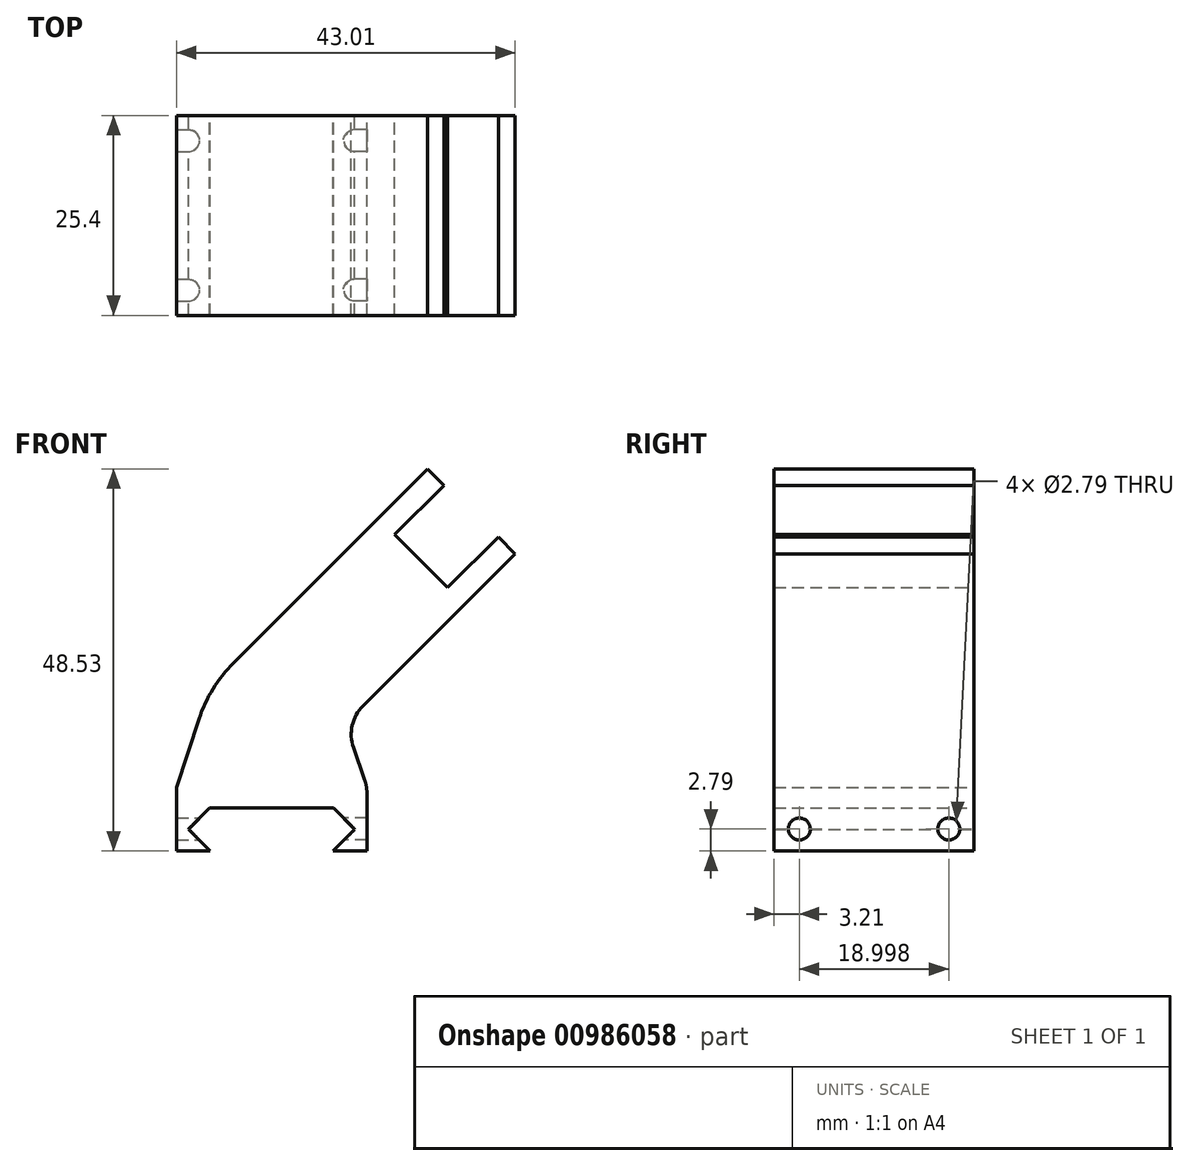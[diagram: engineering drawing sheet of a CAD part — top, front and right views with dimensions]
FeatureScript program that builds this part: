
annotation { "Feature Type Name" : "Feature", "Feature Type Description" : "" }
export const myFeature = defineFeature(function(context is Context, id is Id, definition is map)
    precondition{}
    {
        {
            var Q0;
            Q0=qCreatedBy(makeId("Front.planeOp"),FACE);
            var sketch = newSketch(context, id + "F0", { "sketchPlane" : qUnion([Q0])});
            skLineSegment(sketch, "E0", {"start": v(8.24, -9.31) * mm, "end": v(11, -6.54) * mm});
            skLineSegment(sketch, "E1", {"start": v(11, -6.54) * mm, "end": v(8.23, -3.78) * mm});
            skLineSegment(sketch, "E2.MirrorCS", {"start": v(-10.13, -6.54) * mm, "end": v(-7.35, -3.78) * mm});
            skLineSegment(sketch, "E3.MirrorCS", {"start": v(-7.36, -9.3) * mm, "end": v(-10.13, -6.54) * mm});
            skLineSegment(sketch, "E4.bottom", {"start": v(-7.36, -9.3) * mm, "end": v(-11.63, -9.3) * mm});
            skLineSegment(sketch, "E5.top", {"start": v(8.32, -3.86) * mm, "end": v(-7.44, -3.86) * mm});
            skLineSegment(sketch, "E6.right", {"start": v(-11.63, -1.23) * mm, "end": v(-11.63, -9.3) * mm});
            skLineSegment(sketch, "E7.top", {"start": v(12.55, -9.31) * mm, "end": v(8.24, -9.31) * mm});
            skLineSegment(sketch, "E7.left", {"start": v(12.55, -1.1) * mm, "end": v(12.55, -9.31) * mm});
            skLineSegment(sketch, "E8", {"start": v(9.8, 6.84) * mm, "end": v(12.55, -1.1) * mm});
            skLineSegment(sketch, "E9", {"start": v(-7.44, 11.55) * mm, "end": v(-11.63, -1.23) * mm});
            skLineSegment(sketch, "E10.top", {"start": v(16.07, 30.88) * mm, "end": v(22.8, 24.14) * mm});
            skLineSegment(sketch, "E10.left", {"start": v(-7.44, 11.55) * mm, "end": v(14.03, 33.02) * mm});
            skLineSegment(sketch, "E10.right", {"start": v(9.8, 6.84) * mm, "end": v(24.95, 22) * mm});
            skLineSegment(sketch, "E11.bottom", {"start": v(20.23, 39.22) * mm, "end": v(22.32, 37.13) * mm});
            skLineSegment(sketch, "E11.left", {"start": v(20.23, 39.22) * mm, "end": v(13.98, 32.97) * mm});
            skLineSegment(sketch, "E11.right", {"start": v(22.32, 37.13) * mm, "end": v(16.07, 30.88) * mm});
            skLineSegment(sketch, "E12.bottom", {"start": v(29.24, 30.58) * mm, "end": v(31.38, 28.44) * mm});
            skLineSegment(sketch, "E12.left", {"start": v(29.24, 30.58) * mm, "end": v(22.8, 24.14) * mm});
            skLineSegment(sketch, "E12.right", {"start": v(31.38, 28.44) * mm, "end": v(24.95, 22) * mm});
            skLineSegment(sketch, "E13.trimOffspring", {"start": v(-7.44, -1.2) * mm, "end": v(-7.44, -1.21) * mm});
            skPoint(sketch, "E14.top.end.orphan", {"position": v(-7.44, 8.88) * mm});
            skSolve(sketch);
        }
        {
            var Q0;
            {var subQ8=sQuery(id+"F0.wireOp",EDGE,"6de9e082-5b51-49be-9b5f-76bcd6000eec.right");Q0=makeQuery(id+"F0.imprint","IMPRINT",FACE,{"disambiguationData":[TD([[makeQuery(id+"F0.imprint","IMPRINT",EDGE,{"derivedFrom":subQ8}),1.0]])]});}
            var Q1;
            {var subQ6=sQuery(id+"F0.wireOp",EDGE,"E0");Q1=makeQuery(id+"F0.imprint","IMPRINT",FACE,{"disambiguationData":[TD([[makeQuery(id+"F0.imprint","IMPRINT",EDGE,{"derivedFrom":subQ6}),-1.0]])]});}
            var Q2;
            Q2=makeQuery(id+"F0.imprint","IMPRINT",FACE,{"disambiguationData":[TD([[makeQuery(id+"F0.imprint","IMPRINT",EDGE,{"derivedFrom":sQuery(id+"F0.wireOp",EDGE,"E11.bottom")}),-1.0]])]});
            var Q3;
            Q3=makeQuery(id+"F0.imprint","IMPRINT",FACE,{"disambiguationData":[TD([[makeQuery(id+"F0.imprint","IMPRINT",EDGE,{"derivedFrom":sQuery(id+"F0.wireOp",EDGE,"E12.bottom")}),-1.0]])]});
            extrude(context, id + "F1", {"entities" : qUnion([Q0, Q1, Q2, Q3]), "depth" : 25.4 * mm, "offsetDistance" : 25.4 * mm});
        }
        {
            var Q0;
            Q0=qCreatedBy(makeId("Right.planeOp"),FACE);
            var sketch = newSketch(context, id + "F2", { "sketchPlane" : qUnion([Q0])});
            skPoint(sketch, "E15", {"position": v(-22.19, -6.52) * mm});
            skPoint(sketch, "E16", {"position": v(-3.2, -6.52) * mm});
            skSolve(sketch);
        }
        {
            var Q0;
            Q0=sQuery(id+"F2.wireOp",VERTEX,"E15");
            var Q1;
            Q1=sQuery(id+"F2.wireOp",VERTEX,"E16");
            var Q2;
            Q2=makeQuery(id+"F1.opExtrude","SWEPT_BODY",BODY,{"disambiguationData":[OSD([sQuery(id+"F0.wireOp",EDGE,"E0"),sQuery(id+"F0.wireOp",EDGE,"E1"),sQuery(id+"F0.wireOp",EDGE,"E2.MirrorCS"),sQuery(id+"F0.wireOp",EDGE,"E3.MirrorCS"),sQuery(id+"F0.wireOp",EDGE,"E4.bottom"),sQuery(id+"F0.wireOp",EDGE,"E5.top"),sQuery(id+"F0.wireOp",EDGE,"E6.right"),sQuery(id+"F0.wireOp",EDGE,"E7.top"),sQuery(id+"F0.wireOp",EDGE,"E7.left"),sQuery(id+"F0.wireOp",EDGE,"6de9e082-5b51-49be-9b5f-76bcd6000eec.right"),sQuery(id+"F0.wireOp",EDGE,"E8"),sQuery(id+"F0.wireOp",EDGE,"E9"),sQuery(id+"F0.wireOp",EDGE,"E10.top"),sQuery(id+"F0.wireOp",EDGE,"E10.left"),sQuery(id+"F0.wireOp",EDGE,"E10.right"),sQuery(id+"F0.wireOp",EDGE,"E11.bottom"),sQuery(id+"F0.wireOp",EDGE,"E11.left"),sQuery(id+"F0.wireOp",EDGE,"E11.right"),sQuery(id+"F0.wireOp",EDGE,"E12.bottom"),sQuery(id+"F0.wireOp",EDGE,"E12.left"),sQuery(id+"F0.wireOp",EDGE,"E12.right"),sQuery(id+"F0.wireOp",EDGE,"bc1cf760-3795-42bd-bf48-c28c4e5382b4.trimOffspring")])]});
            hole(context, id + "F3", {"style" : HoleStyle.SIMPLE, "endStyle" : HoleEndStyle.BLIND, "oppositeDirection" : true, "holeDiameter" : 2.8 * mm, "majorDiameter" : 6.35 * mm, "holeDepth" : 25.4 * mm, "isTappedThrough" : true, "tappedDepth" : 12.7 * mm, "tapClearance" : 3, "locations" : qUnion([Q0, Q1]), "scope" : qUnion([Q2])});
        }
        {
            var Q0;
            Q0=sQuery(id+"F2.wireOp",VERTEX,"E16");
            var Q1;
            Q1=sQuery(id+"F2.wireOp",VERTEX,"E15");
            var Q2;
            Q2=makeQuery(id+"F1.opExtrude","SWEPT_BODY",BODY,{"disambiguationData":[OSD([sQuery(id+"F0.wireOp",EDGE,"E0"),sQuery(id+"F0.wireOp",EDGE,"E1"),sQuery(id+"F0.wireOp",EDGE,"E2.MirrorCS"),sQuery(id+"F0.wireOp",EDGE,"E3.MirrorCS"),sQuery(id+"F0.wireOp",EDGE,"E4.bottom"),sQuery(id+"F0.wireOp",EDGE,"E5.top"),sQuery(id+"F0.wireOp",EDGE,"E6.right"),sQuery(id+"F0.wireOp",EDGE,"E7.top"),sQuery(id+"F0.wireOp",EDGE,"E7.left"),sQuery(id+"F0.wireOp",EDGE,"6de9e082-5b51-49be-9b5f-76bcd6000eec.right"),sQuery(id+"F0.wireOp",EDGE,"E8"),sQuery(id+"F0.wireOp",EDGE,"E9"),sQuery(id+"F0.wireOp",EDGE,"E10.top"),sQuery(id+"F0.wireOp",EDGE,"E10.left"),sQuery(id+"F0.wireOp",EDGE,"E10.right"),sQuery(id+"F0.wireOp",EDGE,"E11.bottom"),sQuery(id+"F0.wireOp",EDGE,"E11.left"),sQuery(id+"F0.wireOp",EDGE,"E11.right"),sQuery(id+"F0.wireOp",EDGE,"E12.bottom"),sQuery(id+"F0.wireOp",EDGE,"E12.left"),sQuery(id+"F0.wireOp",EDGE,"E12.right"),sQuery(id+"F0.wireOp",EDGE,"bc1cf760-3795-42bd-bf48-c28c4e5382b4.trimOffspring")])]});
            hole(context, id + "F4", {"style" : HoleStyle.SIMPLE, "endStyle" : HoleEndStyle.BLIND, "holeDiameter" : 2.8 * mm, "majorDiameter" : 6.35 * mm, "holeDepth" : 25.4 * mm, "isTappedThrough" : true, "tappedDepth" : 12.7 * mm, "tapClearance" : 3, "locations" : qUnion([Q0, Q1]), "scope" : qUnion([Q2])});
        }
        {
            var Q0;
            Q0=makeQuery(id+"F1.opExtrude","SWEPT_EDGE",EDGE,{"disambiguationData":[OSD([sQuery(id+"F0.wireOp",EDGE,"E9"),sQuery(id+"F0.wireOp",EDGE,"E10.left")])]});
            fillet(context, id + "F5", {"entities" : qUnion([Q0]), "radius" : 18.09 * mm, "tangentPropagation" : true, "allowEdgeOverflow" : false});
        }
        {
            var Q0;
            Q0=makeQuery(id+"F1.opExtrude","SWEPT_EDGE",EDGE,{"disambiguationData":[OSD([sQuery(id+"F0.wireOp",EDGE,"E8"),sQuery(id+"F0.wireOp",EDGE,"E10.right")])]});
            var Q1;
            Q1=makeQuery(id+"F1.opExtrude","SWEPT_EDGE",EDGE,{"disambiguationData":[OSD([sQuery(id+"F0.wireOp",EDGE,"E7.left"),sQuery(id+"F0.wireOp",EDGE,"E8")])]});
            fillet(context, id + "F6", {"entities" : qUnion([Q0, Q1]), "radius" : 5.08 * mm, "tangentPropagation" : true, "allowEdgeOverflow" : false});
        }
    });
